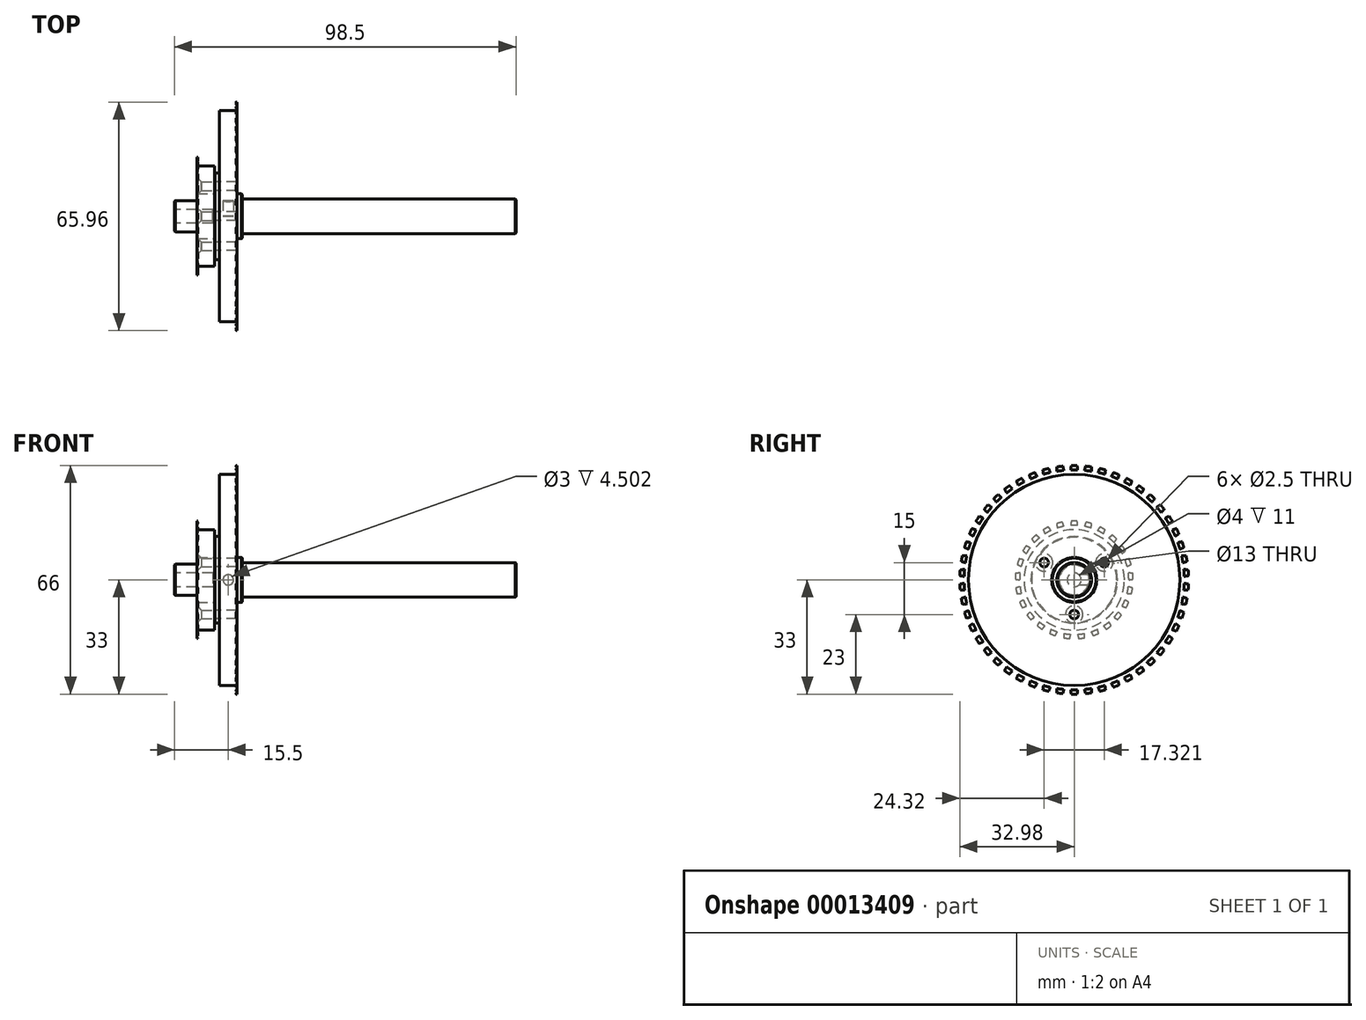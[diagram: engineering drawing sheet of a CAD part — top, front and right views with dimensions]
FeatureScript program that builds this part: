
annotation { "Feature Type Name" : "Feature", "Feature Type Description" : "" }
export const myFeature = defineFeature(function(context is Context, id is Id, definition is map)
    precondition{}
    {
        {
            var Q0;
            Q0=qCreatedBy(makeId("Right.planeOp"),FACE);
            var sketch = newSketch(context, id + "F0", { "sketchPlane" : qUnion([Q0])});
            skCircle(sketch, "E0", {"center": v(0, 0) * mm, "radius": 4.5 * mm});
            skCircle(sketch, "E1", {"center": v(0, 0) * mm, "radius": 5 * mm});
            skSolve(sketch);
        }
        {
            var Q0;
            Q0=makeQuery(id+"F0.imprint","IMPRINT",FACE,{"disambiguationData":[TD([[makeQuery(id+"F0.imprint","IMPRINT",EDGE,{"derivedFrom":sQuery(id+"F0.wireOp",EDGE,"E0")}),1.0]])]});
            extrude(context, id + "F1", {"entities" : qUnion([Q0]), "oppositeDirection" : true, "depth" : 13 * mm});
        }
        {
            var Q0;
            Q0=makeQuery(id+"F0.imprint","IMPRINT",FACE,{"disambiguationData":[TD([[makeQuery(id+"F0.imprint","IMPRINT",EDGE,{"derivedFrom":sQuery(id+"F0.wireOp",EDGE,"E0")}),1.0]])]});
            var Q1;
            Q1=makeQuery(id+"F0.imprint","IMPRINT",FACE,{"disambiguationData":[TD([[makeQuery(id+"F0.imprint","IMPRINT",EDGE,{"derivedFrom":sQuery(id+"F0.wireOp",EDGE,"E0")}),-1.0]])]});
            extrude(context, id + "F2", {"entities" : qUnion([Q0, Q1]), "operationType" : NewBodyOperationType.ADD, "depth" : 85.5 * mm});
        }
        {
            var Q0;
            Q0=makeQuery(id+"F1.opExtrude","CAP_FACE",FACE,{"disambiguationData":[OSD([sQuery(id+"F0.wireOp",EDGE,"E0")])],"isStart":false});
            var sketch = newSketch(context, id + "F3", { "sketchPlane" : qUnion([Q0])});
            skCircle(sketch, "E2", {"center": v(0, 0) * mm, "radius": 2 * mm});
            skSolve(sketch);
        }
        {
            var Q0;
            Q0=makeQuery(id+"F3.imprint","IMPRINT",FACE,{"disambiguationData":[TD([[makeQuery(id+"F3.imprint","IMPRINT",EDGE,{"derivedFrom":sQuery(id+"F3.wireOp",EDGE,"E2")}),1.0]])]});
            extrude(context, id + "F4", {"entities" : qUnion([Q0]), "operationType" : NewBodyOperationType.REMOVE, "oppositeDirection" : true, "depth" : 11 * mm});
        }
        {
            var Q0;
            Q0=makeQuery(id+"F2.opExtrude","CAP_FACE",FACE,{"disambiguationData":[OSD([sQuery(id+"F0.wireOp",EDGE,"E1")])],"isStart":true});
            var sketch = newSketch(context, id + "F5", { "sketchPlane" : qUnion([Q0])});
            skCircle(sketch, "E3", {"center": v(0, 0) * mm, "radius": 8 * mm});
            skSolve(sketch);
        }
        {
            var Q0;
            Q0=makeQuery(id+"F5.imprint","IMPRINT",FACE,{"disambiguationData":[TD([[makeQuery(id+"F5.imprint","IMPRINT",EDGE,{"derivedFrom":sQuery(id+"F5.wireOp",EDGE,"E3")}),1.0]])]});
            extrude(context, id + "F6", {"entities" : qUnion([Q0]), "oppositeDirection" : true, "depth" : 5 * mm});
        }
        {
            var Q0;
            Q0=qCreatedBy(makeId("Front.planeOp"),FACE);
            var sketch = newSketch(context, id + "F7", { "sketchPlane" : qUnion([Q0])});
            skLineSegment(sketch, "E4.0", {"start": v(0, -8) * mm, "end": v(0, 8) * mm});
            skLineSegment(sketch, "E4.1", {"start": v(5, -8) * mm, "end": v(5, 8) * mm});
            skLineSegment(sketch, "E5", {"start": v(5, 0) * mm, "end": v(0, 0) * mm, "construction": true});
            skCircle(sketch, "E6", {"center": v(2.5, 0) * mm, "radius": 1.5 * mm});
            skSolve(sketch);
        }
        {
            var Q0;
            Q0=makeQuery(id+"F7.imprint","IMPRINT",FACE,{"disambiguationData":[TD([[makeQuery(id+"F7.imprint","IMPRINT",EDGE,{"derivedFrom":sQuery(id+"F7.wireOp",EDGE,"E6")}),1.0]])]});
            extrude(context, id + "F8", {"entities" : qUnion([Q0]), "operationType" : NewBodyOperationType.REMOVE, "oppositeDirection" : true, "depth" : 8 * mm});
        }
        {
            var Q0;
            Q0=makeQuery(id+"F6.opExtrude","CAP_FACE",FACE,{"disambiguationData":[OSD([sQuery(id+"F0.wireOp",EDGE,"E1"),sQuery(id+"F5.wireOp",EDGE,"E3")])],"isStart":true});
            var sketch = newSketch(context, id + "F9", { "sketchPlane" : qUnion([Q0])});
            skCircle(sketch, "E7", {"center": v(0, 0) * mm, "radius": 30.5 * mm});
            skCircle(sketch, "E8", {"center": v(0, 0) * mm, "radius": 33 * mm});
            skCircle(sketch, "E9", {"center": v(0, 0) * mm, "radius": 31.75 * mm, "construction": true});
            skLineSegment(sketch, "E10", {"start": v(0, 0) * mm, "end": v(0, 33) * mm, "construction": true});
            skLineSegment(sketch, "E11", {"start": v(0, 0) * mm, "end": v(-1, 31.73) * mm, "construction": true});
            skLineSegment(sketch, "E12", {"start": v(0, 0) * mm, "end": v(0, -10) * mm, "construction": true});
            skCircle(sketch, "E13", {"center": v(0, -10) * mm, "radius": 1.25 * mm});
            skCircle(sketch, "E14.1.0", {"center": v(8.66, 5) * mm, "radius": 1.25 * mm});
            skCircle(sketch, "E14.2.0", {"center": v(-8.66, 5) * mm, "radius": 1.25 * mm});
            skLineSegment(sketch, "E15", {"start": v(0, 30.5) * mm, "end": v(15, 30.5) * mm, "construction": true});
            skArc(sketch, "E16", {"start": v(-0.85, 32.99) * mm, "mid": v(-1, 31.74) * mm, "end": v(-1.04, 30.48) * mm});
            skArc(sketch, "E17.0.MirrorCS", {"start": v(0.85, 32.99) * mm, "mid": v(1, 31.74) * mm, "end": v(1.04, 30.48) * mm});
            skArc(sketch, "E18.1.0", {"start": v(-4.98, 32.62) * mm, "mid": v(-4.97, 31.36) * mm, "end": v(-4.86, 30.11) * mm});
            skArc(sketch, "E18.1.1", {"start": v(-3.3, 32.84) * mm, "mid": v(-2.99, 31.61) * mm, "end": v(-2.78, 30.37) * mm});
            skArc(sketch, "E18.2.0", {"start": v(-9.03, 31.74) * mm, "mid": v(-8.86, 30.5) * mm, "end": v(-8.6, 29.26) * mm});
            skArc(sketch, "E18.2.1", {"start": v(-7.38, 32.16) * mm, "mid": v(-6.93, 31) * mm, "end": v(-6.57, 29.78) * mm});
            skArc(sketch, "E18.3.0", {"start": v(-12.93, 30.36) * mm, "mid": v(-12.61, 29.14) * mm, "end": v(-12.2, 27.96) * mm});
            skArc(sketch, "E18.3.1", {"start": v(-11.35, 30.99) * mm, "mid": v(-10.76, 29.88) * mm, "end": v(-10.25, 28.73) * mm});
            skArc(sketch, "E18.4.0", {"start": v(-16.64, 28.5) * mm, "mid": v(-16.16, 27.33) * mm, "end": v(-15.6, 26.2) * mm});
            skArc(sketch, "E18.4.1", {"start": v(-15.15, 29.32) * mm, "mid": v(-14.42, 28.3) * mm, "end": v(-13.77, 27.22) * mm});
            skArc(sketch, "E18.5.0", {"start": v(-20.08, 26.19) * mm, "mid": v(-19.46, 25.1) * mm, "end": v(-18.76, 24.05) * mm});
            skArc(sketch, "E18.5.1", {"start": v(-18.7, 27.19) * mm, "mid": v(-17.85, 26.26) * mm, "end": v(-17.07, 25.27) * mm});
            skArc(sketch, "E18.6.0", {"start": v(-23.2, 23.47) * mm, "mid": v(-22.45, 22.45) * mm, "end": v(-21.63, 21.5) * mm});
            skArc(sketch, "E18.6.1", {"start": v(-21.96, 24.63) * mm, "mid": v(-21, 23.82) * mm, "end": v(-20.1, 22.94) * mm});
            skArc(sketch, "E18.7.0", {"start": v(-25.96, 20.37) * mm, "mid": v(-25.1, 19.46) * mm, "end": v(-24.15, 18.62) * mm});
            skArc(sketch, "E18.7.1", {"start": v(-24.88, 21.68) * mm, "mid": v(-23.82, 21) * mm, "end": v(-22.82, 20.24) * mm});
            skArc(sketch, "E18.8.0", {"start": v(-28.3, 16.96) * mm, "mid": v(-27.33, 16.17) * mm, "end": v(-26.3, 15.45) * mm});
            skArc(sketch, "E18.8.1", {"start": v(-27.4, 18.4) * mm, "mid": v(-26.26, 17.85) * mm, "end": v(-25.18, 17.22) * mm});
            skArc(sketch, "E18.9.0", {"start": v(-30.21, 13.28) * mm, "mid": v(-29.14, 12.61) * mm, "end": v(-28.03, 12.03) * mm});
            skArc(sketch, "E18.9.1", {"start": v(-29.49, 14.82) * mm, "mid": v(-28.3, 14.42) * mm, "end": v(-27.14, 13.92) * mm});
            skArc(sketch, "E18.10.0", {"start": v(-31.64, 9.39) * mm, "mid": v(-30.5, 8.86) * mm, "end": v(-29.31, 8.43) * mm});
            skArc(sketch, "E18.10.1", {"start": v(-31.11, 11) * mm, "mid": v(-29.88, 10.76) * mm, "end": v(-28.67, 10.41) * mm});
            skArc(sketch, "E18.11.0", {"start": v(-32.56, 5.35) * mm, "mid": v(-31.36, 4.97) * mm, "end": v(-30.14, 4.69) * mm});
            skArc(sketch, "E18.11.1", {"start": v(-32.25, 7.02) * mm, "mid": v(-31, 6.93) * mm, "end": v(-29.75, 6.74) * mm});
            skArc(sketch, "E18.12.0", {"start": v(-32.98, 1.22) * mm, "mid": v(-31.74, 1) * mm, "end": v(-30.49, 0.87) * mm});
            skArc(sketch, "E18.12.1", {"start": v(-32.87, 2.92) * mm, "mid": v(-31.61, 2.99) * mm, "end": v(-30.36, 2.96) * mm});
            skArc(sketch, "E18.13.0", {"start": v(-32.87, -2.92) * mm, "mid": v(-31.61, -2.99) * mm, "end": v(-30.36, -2.96) * mm});
            skArc(sketch, "E18.13.1", {"start": v(-32.98, -1.22) * mm, "mid": v(-31.74, -1) * mm, "end": v(-30.49, -0.87) * mm});
            skArc(sketch, "E18.14.0", {"start": v(-32.25, -7.02) * mm, "mid": v(-31, -6.93) * mm, "end": v(-29.75, -6.74) * mm});
            skArc(sketch, "E18.14.1", {"start": v(-32.56, -5.35) * mm, "mid": v(-31.36, -4.97) * mm, "end": v(-30.14, -4.69) * mm});
            skArc(sketch, "E18.15.0", {"start": v(-31.11, -11) * mm, "mid": v(-29.88, -10.76) * mm, "end": v(-28.67, -10.41) * mm});
            skArc(sketch, "E18.15.1", {"start": v(-31.64, -9.39) * mm, "mid": v(-30.5, -8.86) * mm, "end": v(-29.31, -8.43) * mm});
            skArc(sketch, "E18.16.0", {"start": v(-29.49, -14.82) * mm, "mid": v(-28.3, -14.42) * mm, "end": v(-27.14, -13.92) * mm});
            skArc(sketch, "E18.16.1", {"start": v(-30.21, -13.28) * mm, "mid": v(-29.14, -12.61) * mm, "end": v(-28.03, -12.03) * mm});
            skArc(sketch, "E18.17.0", {"start": v(-27.4, -18.4) * mm, "mid": v(-26.26, -17.85) * mm, "end": v(-25.18, -17.22) * mm});
            skArc(sketch, "E18.17.1", {"start": v(-28.3, -16.96) * mm, "mid": v(-27.33, -16.17) * mm, "end": v(-26.3, -15.45) * mm});
            skArc(sketch, "E18.18.0", {"start": v(-24.88, -21.68) * mm, "mid": v(-23.82, -21) * mm, "end": v(-22.82, -20.24) * mm});
            skArc(sketch, "E18.18.1", {"start": v(-25.96, -20.37) * mm, "mid": v(-25.1, -19.46) * mm, "end": v(-24.15, -18.62) * mm});
            skArc(sketch, "E18.19.0", {"start": v(-21.96, -24.63) * mm, "mid": v(-21, -23.82) * mm, "end": v(-20.1, -22.94) * mm});
            skArc(sketch, "E18.19.1", {"start": v(-23.2, -23.47) * mm, "mid": v(-22.45, -22.45) * mm, "end": v(-21.63, -21.5) * mm});
            skArc(sketch, "E18.20.0", {"start": v(-18.7, -27.19) * mm, "mid": v(-17.85, -26.26) * mm, "end": v(-17.07, -25.27) * mm});
            skArc(sketch, "E18.20.1", {"start": v(-20.08, -26.19) * mm, "mid": v(-19.46, -25.1) * mm, "end": v(-18.76, -24.05) * mm});
            skArc(sketch, "E18.21.0", {"start": v(-15.15, -29.32) * mm, "mid": v(-14.42, -28.3) * mm, "end": v(-13.77, -27.22) * mm});
            skArc(sketch, "E18.21.1", {"start": v(-16.64, -28.5) * mm, "mid": v(-16.16, -27.33) * mm, "end": v(-15.6, -26.2) * mm});
            skArc(sketch, "E18.22.0", {"start": v(-11.35, -30.99) * mm, "mid": v(-10.76, -29.88) * mm, "end": v(-10.25, -28.73) * mm});
            skArc(sketch, "E18.22.1", {"start": v(-12.93, -30.36) * mm, "mid": v(-12.61, -29.14) * mm, "end": v(-12.2, -27.96) * mm});
            skArc(sketch, "E18.23.0", {"start": v(-7.38, -32.16) * mm, "mid": v(-6.93, -31) * mm, "end": v(-6.57, -29.78) * mm});
            skArc(sketch, "E18.23.1", {"start": v(-9.03, -31.74) * mm, "mid": v(-8.86, -30.5) * mm, "end": v(-8.6, -29.26) * mm});
            skArc(sketch, "E18.24.0", {"start": v(-3.3, -32.84) * mm, "mid": v(-2.99, -31.61) * mm, "end": v(-2.78, -30.37) * mm});
            skArc(sketch, "E18.24.1", {"start": v(-4.98, -32.62) * mm, "mid": v(-4.97, -31.36) * mm, "end": v(-4.86, -30.11) * mm});
            skArc(sketch, "E18.25.0", {"start": v(0.85, -32.99) * mm, "mid": v(1, -31.74) * mm, "end": v(1.04, -30.48) * mm});
            skArc(sketch, "E18.25.1", {"start": v(-0.85, -32.99) * mm, "mid": v(-1, -31.74) * mm, "end": v(-1.04, -30.48) * mm});
            skArc(sketch, "E18.26.0", {"start": v(4.98, -32.62) * mm, "mid": v(4.97, -31.36) * mm, "end": v(4.86, -30.11) * mm});
            skArc(sketch, "E18.26.1", {"start": v(3.3, -32.84) * mm, "mid": v(2.99, -31.61) * mm, "end": v(2.78, -30.37) * mm});
            skArc(sketch, "E18.27.0", {"start": v(9.03, -31.74) * mm, "mid": v(8.86, -30.5) * mm, "end": v(8.6, -29.26) * mm});
            skArc(sketch, "E18.27.1", {"start": v(7.38, -32.16) * mm, "mid": v(6.93, -31) * mm, "end": v(6.57, -29.78) * mm});
            skArc(sketch, "E18.28.0", {"start": v(12.93, -30.36) * mm, "mid": v(12.61, -29.14) * mm, "end": v(12.2, -27.96) * mm});
            skArc(sketch, "E18.28.1", {"start": v(11.35, -30.99) * mm, "mid": v(10.76, -29.88) * mm, "end": v(10.25, -28.73) * mm});
            skArc(sketch, "E18.29.0", {"start": v(16.64, -28.5) * mm, "mid": v(16.16, -27.33) * mm, "end": v(15.6, -26.2) * mm});
            skArc(sketch, "E18.29.1", {"start": v(15.15, -29.32) * mm, "mid": v(14.42, -28.3) * mm, "end": v(13.77, -27.22) * mm});
            skArc(sketch, "E18.30.0", {"start": v(20.08, -26.19) * mm, "mid": v(19.46, -25.1) * mm, "end": v(18.76, -24.05) * mm});
            skArc(sketch, "E18.30.1", {"start": v(18.7, -27.19) * mm, "mid": v(17.85, -26.26) * mm, "end": v(17.07, -25.27) * mm});
            skArc(sketch, "E18.31.0", {"start": v(23.2, -23.47) * mm, "mid": v(22.45, -22.45) * mm, "end": v(21.63, -21.5) * mm});
            skArc(sketch, "E18.31.1", {"start": v(21.96, -24.63) * mm, "mid": v(21, -23.82) * mm, "end": v(20.1, -22.94) * mm});
            skArc(sketch, "E18.32.0", {"start": v(25.96, -20.37) * mm, "mid": v(25.1, -19.46) * mm, "end": v(24.15, -18.62) * mm});
            skArc(sketch, "E18.32.1", {"start": v(24.88, -21.68) * mm, "mid": v(23.82, -21) * mm, "end": v(22.82, -20.24) * mm});
            skArc(sketch, "E18.33.0", {"start": v(28.3, -16.96) * mm, "mid": v(27.33, -16.17) * mm, "end": v(26.3, -15.45) * mm});
            skArc(sketch, "E18.33.1", {"start": v(27.4, -18.4) * mm, "mid": v(26.26, -17.85) * mm, "end": v(25.18, -17.22) * mm});
            skArc(sketch, "E18.34.0", {"start": v(30.21, -13.28) * mm, "mid": v(29.14, -12.61) * mm, "end": v(28.03, -12.03) * mm});
            skArc(sketch, "E18.34.1", {"start": v(29.49, -14.82) * mm, "mid": v(28.3, -14.42) * mm, "end": v(27.14, -13.92) * mm});
            skArc(sketch, "E18.35.0", {"start": v(31.64, -9.39) * mm, "mid": v(30.5, -8.86) * mm, "end": v(29.31, -8.43) * mm});
            skArc(sketch, "E18.35.1", {"start": v(31.11, -11) * mm, "mid": v(29.88, -10.76) * mm, "end": v(28.67, -10.41) * mm});
            skArc(sketch, "E18.36.0", {"start": v(32.56, -5.35) * mm, "mid": v(31.36, -4.97) * mm, "end": v(30.14, -4.69) * mm});
            skArc(sketch, "E18.36.1", {"start": v(32.25, -7.02) * mm, "mid": v(31, -6.93) * mm, "end": v(29.75, -6.74) * mm});
            skArc(sketch, "E18.37.0", {"start": v(32.98, -1.22) * mm, "mid": v(31.74, -1) * mm, "end": v(30.49, -0.87) * mm});
            skArc(sketch, "E18.37.1", {"start": v(32.87, -2.92) * mm, "mid": v(31.61, -2.99) * mm, "end": v(30.36, -2.96) * mm});
            skArc(sketch, "E18.38.0", {"start": v(32.87, 2.92) * mm, "mid": v(31.61, 2.99) * mm, "end": v(30.36, 2.96) * mm});
            skArc(sketch, "E18.38.1", {"start": v(32.98, 1.22) * mm, "mid": v(31.74, 1) * mm, "end": v(30.49, 0.87) * mm});
            skArc(sketch, "E18.39.0", {"start": v(32.25, 7.02) * mm, "mid": v(31, 6.93) * mm, "end": v(29.75, 6.74) * mm});
            skArc(sketch, "E18.39.1", {"start": v(32.56, 5.35) * mm, "mid": v(31.36, 4.97) * mm, "end": v(30.14, 4.69) * mm});
            skArc(sketch, "E18.40.0", {"start": v(31.11, 11) * mm, "mid": v(29.88, 10.76) * mm, "end": v(28.67, 10.41) * mm});
            skArc(sketch, "E18.40.1", {"start": v(31.64, 9.39) * mm, "mid": v(30.5, 8.86) * mm, "end": v(29.31, 8.43) * mm});
            skArc(sketch, "E18.41.0", {"start": v(29.49, 14.82) * mm, "mid": v(28.3, 14.42) * mm, "end": v(27.14, 13.92) * mm});
            skArc(sketch, "E18.41.1", {"start": v(30.21, 13.28) * mm, "mid": v(29.14, 12.61) * mm, "end": v(28.03, 12.03) * mm});
            skArc(sketch, "E18.42.0", {"start": v(27.4, 18.4) * mm, "mid": v(26.26, 17.85) * mm, "end": v(25.18, 17.22) * mm});
            skArc(sketch, "E18.42.1", {"start": v(28.3, 16.96) * mm, "mid": v(27.33, 16.17) * mm, "end": v(26.3, 15.45) * mm});
            skArc(sketch, "E18.43.0", {"start": v(24.88, 21.68) * mm, "mid": v(23.82, 21) * mm, "end": v(22.82, 20.24) * mm});
            skArc(sketch, "E18.43.1", {"start": v(25.96, 20.37) * mm, "mid": v(25.1, 19.46) * mm, "end": v(24.15, 18.62) * mm});
            skArc(sketch, "E18.44.0", {"start": v(21.96, 24.63) * mm, "mid": v(21, 23.82) * mm, "end": v(20.1, 22.94) * mm});
            skArc(sketch, "E18.44.1", {"start": v(23.2, 23.47) * mm, "mid": v(22.45, 22.45) * mm, "end": v(21.63, 21.5) * mm});
            skArc(sketch, "E18.45.0", {"start": v(18.7, 27.19) * mm, "mid": v(17.85, 26.26) * mm, "end": v(17.07, 25.27) * mm});
            skArc(sketch, "E18.45.1", {"start": v(20.08, 26.19) * mm, "mid": v(19.46, 25.1) * mm, "end": v(18.76, 24.05) * mm});
            skArc(sketch, "E18.46.0", {"start": v(15.15, 29.32) * mm, "mid": v(14.42, 28.3) * mm, "end": v(13.77, 27.22) * mm});
            skArc(sketch, "E18.46.1", {"start": v(16.64, 28.5) * mm, "mid": v(16.16, 27.33) * mm, "end": v(15.6, 26.2) * mm});
            skArc(sketch, "E18.47.0", {"start": v(11.35, 30.99) * mm, "mid": v(10.76, 29.88) * mm, "end": v(10.25, 28.73) * mm});
            skArc(sketch, "E18.47.1", {"start": v(12.93, 30.36) * mm, "mid": v(12.61, 29.14) * mm, "end": v(12.2, 27.96) * mm});
            skArc(sketch, "E18.48.0", {"start": v(7.38, 32.16) * mm, "mid": v(6.93, 31) * mm, "end": v(6.57, 29.78) * mm});
            skArc(sketch, "E18.48.1", {"start": v(9.03, 31.74) * mm, "mid": v(8.86, 30.5) * mm, "end": v(8.6, 29.26) * mm});
            skArc(sketch, "E18.49.0", {"start": v(3.3, 32.84) * mm, "mid": v(2.99, 31.61) * mm, "end": v(2.78, 30.37) * mm});
            skArc(sketch, "E18.49.1", {"start": v(4.98, 32.62) * mm, "mid": v(4.97, 31.36) * mm, "end": v(4.86, 30.11) * mm});
            skSolve(sketch);
        }
        {
            var Q0;
            Q0=makeQuery(id+"F9.imprint","IMPRINT",FACE,{"disambiguationData":[TD([[makeQuery(id+"F9.imprint","IMPRINT",EDGE,{"derivedFrom":sQuery(id+"F9.wireOp",EDGE,"E13")}),-1.0]])]});
            var Q1;
            {var subQ1=sQuery(id+"F9.wireOp",EDGE,"E16");Q1=makeQuery(id+"F9.imprint","IMPRINT",FACE,{"disambiguationData":[TD([[makeQuery(id+"F9.imprint","IMPRINT",EDGE,{"derivedFrom":subQ1}),1.0]])]});}
            var Q2;
            {var subQ1=sQuery(id+"F9.wireOp",EDGE,"E18.1.0");Q2=makeQuery(id+"F9.imprint","IMPRINT",FACE,{"disambiguationData":[TD([[makeQuery(id+"F9.imprint","IMPRINT",EDGE,{"derivedFrom":subQ1}),1.0]])]});}
            var Q3;
            {var subQ1=sQuery(id+"F9.wireOp",EDGE,"E18.2.0");Q3=makeQuery(id+"F9.imprint","IMPRINT",FACE,{"disambiguationData":[TD([[makeQuery(id+"F9.imprint","IMPRINT",EDGE,{"derivedFrom":subQ1}),1.0]])]});}
            var Q4;
            {var subQ2=sQuery(id+"F9.wireOp",EDGE,"E18.3.0");Q4=makeQuery(id+"F9.imprint","IMPRINT",FACE,{"disambiguationData":[TD([[makeQuery(id+"F9.imprint","IMPRINT",EDGE,{"derivedFrom":subQ2}),1.0]])]});}
            var Q5;
            {var subQ1=sQuery(id+"F9.wireOp",EDGE,"E18.4.0");Q5=makeQuery(id+"F9.imprint","IMPRINT",FACE,{"disambiguationData":[TD([[makeQuery(id+"F9.imprint","IMPRINT",EDGE,{"derivedFrom":subQ1}),1.0]])]});}
            var Q6;
            {var subQ1=sQuery(id+"F9.wireOp",EDGE,"E18.5.0");Q6=makeQuery(id+"F9.imprint","IMPRINT",FACE,{"disambiguationData":[TD([[makeQuery(id+"F9.imprint","IMPRINT",EDGE,{"derivedFrom":subQ1}),1.0]])]});}
            var Q7;
            {var subQ1=sQuery(id+"F9.wireOp",EDGE,"E18.6.0");Q7=makeQuery(id+"F9.imprint","IMPRINT",FACE,{"disambiguationData":[TD([[makeQuery(id+"F9.imprint","IMPRINT",EDGE,{"derivedFrom":subQ1}),1.0]])]});}
            var Q8;
            {var subQ1=sQuery(id+"F9.wireOp",EDGE,"E18.7.0");Q8=makeQuery(id+"F9.imprint","IMPRINT",FACE,{"disambiguationData":[TD([[makeQuery(id+"F9.imprint","IMPRINT",EDGE,{"derivedFrom":subQ1}),1.0]])]});}
            var Q9;
            {var subQ1=sQuery(id+"F9.wireOp",EDGE,"E18.8.0");Q9=makeQuery(id+"F9.imprint","IMPRINT",FACE,{"disambiguationData":[TD([[makeQuery(id+"F9.imprint","IMPRINT",EDGE,{"derivedFrom":subQ1}),1.0]])]});}
            var Q10;
            {var subQ1=sQuery(id+"F9.wireOp",EDGE,"E18.9.0");Q10=makeQuery(id+"F9.imprint","IMPRINT",FACE,{"disambiguationData":[TD([[makeQuery(id+"F9.imprint","IMPRINT",EDGE,{"derivedFrom":subQ1}),1.0]])]});}
            var Q11;
            {var subQ1=sQuery(id+"F9.wireOp",EDGE,"E18.10.0");Q11=makeQuery(id+"F9.imprint","IMPRINT",FACE,{"disambiguationData":[TD([[makeQuery(id+"F9.imprint","IMPRINT",EDGE,{"derivedFrom":subQ1}),1.0]])]});}
            var Q12;
            {var subQ1=sQuery(id+"F9.wireOp",EDGE,"E18.11.0");Q12=makeQuery(id+"F9.imprint","IMPRINT",FACE,{"disambiguationData":[TD([[makeQuery(id+"F9.imprint","IMPRINT",EDGE,{"derivedFrom":subQ1}),1.0]])]});}
            var Q13;
            {var subQ1=sQuery(id+"F9.wireOp",EDGE,"E18.12.0");Q13=makeQuery(id+"F9.imprint","IMPRINT",FACE,{"disambiguationData":[TD([[makeQuery(id+"F9.imprint","IMPRINT",EDGE,{"derivedFrom":subQ1}),1.0]])]});}
            var Q14;
            {var subQ1=sQuery(id+"F9.wireOp",EDGE,"E18.13.0");Q14=makeQuery(id+"F9.imprint","IMPRINT",FACE,{"disambiguationData":[TD([[makeQuery(id+"F9.imprint","IMPRINT",EDGE,{"derivedFrom":subQ1}),1.0]])]});}
            var Q15;
            {var subQ1=sQuery(id+"F9.wireOp",EDGE,"E18.14.0");Q15=makeQuery(id+"F9.imprint","IMPRINT",FACE,{"disambiguationData":[TD([[makeQuery(id+"F9.imprint","IMPRINT",EDGE,{"derivedFrom":subQ1}),1.0]])]});}
            var Q16;
            {var subQ1=sQuery(id+"F9.wireOp",EDGE,"E18.15.0");Q16=makeQuery(id+"F9.imprint","IMPRINT",FACE,{"disambiguationData":[TD([[makeQuery(id+"F9.imprint","IMPRINT",EDGE,{"derivedFrom":subQ1}),1.0]])]});}
            var Q17;
            {var subQ1=sQuery(id+"F9.wireOp",EDGE,"E18.16.0");Q17=makeQuery(id+"F9.imprint","IMPRINT",FACE,{"disambiguationData":[TD([[makeQuery(id+"F9.imprint","IMPRINT",EDGE,{"derivedFrom":subQ1}),1.0]])]});}
            var Q18;
            {var subQ1=sQuery(id+"F9.wireOp",EDGE,"E18.17.0");Q18=makeQuery(id+"F9.imprint","IMPRINT",FACE,{"disambiguationData":[TD([[makeQuery(id+"F9.imprint","IMPRINT",EDGE,{"derivedFrom":subQ1}),1.0]])]});}
            var Q19;
            {var subQ1=sQuery(id+"F9.wireOp",EDGE,"E18.18.0");Q19=makeQuery(id+"F9.imprint","IMPRINT",FACE,{"disambiguationData":[TD([[makeQuery(id+"F9.imprint","IMPRINT",EDGE,{"derivedFrom":subQ1}),1.0]])]});}
            var Q20;
            {var subQ2=sQuery(id+"F9.wireOp",EDGE,"E18.19.0");Q20=makeQuery(id+"F9.imprint","IMPRINT",FACE,{"disambiguationData":[TD([[makeQuery(id+"F9.imprint","IMPRINT",EDGE,{"derivedFrom":subQ2}),1.0]])]});}
            var Q21;
            {var subQ1=sQuery(id+"F9.wireOp",EDGE,"E18.20.0");Q21=makeQuery(id+"F9.imprint","IMPRINT",FACE,{"disambiguationData":[TD([[makeQuery(id+"F9.imprint","IMPRINT",EDGE,{"derivedFrom":subQ1}),1.0]])]});}
            var Q22;
            {var subQ1=sQuery(id+"F9.wireOp",EDGE,"E18.21.0");Q22=makeQuery(id+"F9.imprint","IMPRINT",FACE,{"disambiguationData":[TD([[makeQuery(id+"F9.imprint","IMPRINT",EDGE,{"derivedFrom":subQ1}),1.0]])]});}
            var Q23;
            {var subQ1=sQuery(id+"F9.wireOp",EDGE,"E18.22.0");Q23=makeQuery(id+"F9.imprint","IMPRINT",FACE,{"disambiguationData":[TD([[makeQuery(id+"F9.imprint","IMPRINT",EDGE,{"derivedFrom":subQ1}),1.0]])]});}
            var Q24;
            {var subQ1=sQuery(id+"F9.wireOp",EDGE,"E18.23.0");Q24=makeQuery(id+"F9.imprint","IMPRINT",FACE,{"disambiguationData":[TD([[makeQuery(id+"F9.imprint","IMPRINT",EDGE,{"derivedFrom":subQ1}),1.0]])]});}
            var Q25;
            {var subQ1=sQuery(id+"F9.wireOp",EDGE,"E18.24.0");Q25=makeQuery(id+"F9.imprint","IMPRINT",FACE,{"disambiguationData":[TD([[makeQuery(id+"F9.imprint","IMPRINT",EDGE,{"derivedFrom":subQ1}),1.0]])]});}
            var Q26;
            {var subQ1=sQuery(id+"F9.wireOp",EDGE,"E18.25.0");Q26=makeQuery(id+"F9.imprint","IMPRINT",FACE,{"disambiguationData":[TD([[makeQuery(id+"F9.imprint","IMPRINT",EDGE,{"derivedFrom":subQ1}),1.0]])]});}
            var Q27;
            {var subQ1=sQuery(id+"F9.wireOp",EDGE,"E18.26.0");Q27=makeQuery(id+"F9.imprint","IMPRINT",FACE,{"disambiguationData":[TD([[makeQuery(id+"F9.imprint","IMPRINT",EDGE,{"derivedFrom":subQ1}),1.0]])]});}
            var Q28;
            {var subQ2=sQuery(id+"F9.wireOp",EDGE,"E18.27.0");Q28=makeQuery(id+"F9.imprint","IMPRINT",FACE,{"disambiguationData":[TD([[makeQuery(id+"F9.imprint","IMPRINT",EDGE,{"derivedFrom":subQ2}),1.0]])]});}
            var Q29;
            {var subQ1=sQuery(id+"F9.wireOp",EDGE,"E18.28.0");Q29=makeQuery(id+"F9.imprint","IMPRINT",FACE,{"disambiguationData":[TD([[makeQuery(id+"F9.imprint","IMPRINT",EDGE,{"derivedFrom":subQ1}),1.0]])]});}
            var Q30;
            {var subQ1=sQuery(id+"F9.wireOp",EDGE,"E18.29.0");Q30=makeQuery(id+"F9.imprint","IMPRINT",FACE,{"disambiguationData":[TD([[makeQuery(id+"F9.imprint","IMPRINT",EDGE,{"derivedFrom":subQ1}),1.0]])]});}
            var Q31;
            {var subQ1=sQuery(id+"F9.wireOp",EDGE,"E18.30.0");Q31=makeQuery(id+"F9.imprint","IMPRINT",FACE,{"disambiguationData":[TD([[makeQuery(id+"F9.imprint","IMPRINT",EDGE,{"derivedFrom":subQ1}),1.0]])]});}
            var Q32;
            {var subQ1=sQuery(id+"F9.wireOp",EDGE,"E18.31.0");Q32=makeQuery(id+"F9.imprint","IMPRINT",FACE,{"disambiguationData":[TD([[makeQuery(id+"F9.imprint","IMPRINT",EDGE,{"derivedFrom":subQ1}),1.0]])]});}
            var Q33;
            {var subQ1=sQuery(id+"F9.wireOp",EDGE,"E18.32.0");Q33=makeQuery(id+"F9.imprint","IMPRINT",FACE,{"disambiguationData":[TD([[makeQuery(id+"F9.imprint","IMPRINT",EDGE,{"derivedFrom":subQ1}),1.0]])]});}
            var Q34;
            {var subQ1=sQuery(id+"F9.wireOp",EDGE,"E18.33.0");Q34=makeQuery(id+"F9.imprint","IMPRINT",FACE,{"disambiguationData":[TD([[makeQuery(id+"F9.imprint","IMPRINT",EDGE,{"derivedFrom":subQ1}),1.0]])]});}
            var Q35;
            {var subQ1=sQuery(id+"F9.wireOp",EDGE,"E18.34.0");Q35=makeQuery(id+"F9.imprint","IMPRINT",FACE,{"disambiguationData":[TD([[makeQuery(id+"F9.imprint","IMPRINT",EDGE,{"derivedFrom":subQ1}),1.0]])]});}
            var Q36;
            {var subQ2=sQuery(id+"F9.wireOp",EDGE,"E18.35.0");Q36=makeQuery(id+"F9.imprint","IMPRINT",FACE,{"disambiguationData":[TD([[makeQuery(id+"F9.imprint","IMPRINT",EDGE,{"derivedFrom":subQ2}),1.0]])]});}
            var Q37;
            {var subQ1=sQuery(id+"F9.wireOp",EDGE,"E18.36.0");Q37=makeQuery(id+"F9.imprint","IMPRINT",FACE,{"disambiguationData":[TD([[makeQuery(id+"F9.imprint","IMPRINT",EDGE,{"derivedFrom":subQ1}),1.0]])]});}
            var Q38;
            {var subQ1=sQuery(id+"F9.wireOp",EDGE,"E18.37.0");Q38=makeQuery(id+"F9.imprint","IMPRINT",FACE,{"disambiguationData":[TD([[makeQuery(id+"F9.imprint","IMPRINT",EDGE,{"derivedFrom":subQ1}),1.0]])]});}
            var Q39;
            {var subQ1=sQuery(id+"F9.wireOp",EDGE,"E18.38.0");Q39=makeQuery(id+"F9.imprint","IMPRINT",FACE,{"disambiguationData":[TD([[makeQuery(id+"F9.imprint","IMPRINT",EDGE,{"derivedFrom":subQ1}),1.0]])]});}
            var Q40;
            {var subQ2=sQuery(id+"F9.wireOp",EDGE,"E18.39.0");Q40=makeQuery(id+"F9.imprint","IMPRINT",FACE,{"disambiguationData":[TD([[makeQuery(id+"F9.imprint","IMPRINT",EDGE,{"derivedFrom":subQ2}),1.0]])]});}
            var Q41;
            {var subQ2=sQuery(id+"F9.wireOp",EDGE,"E18.40.0");Q41=makeQuery(id+"F9.imprint","IMPRINT",FACE,{"disambiguationData":[TD([[makeQuery(id+"F9.imprint","IMPRINT",EDGE,{"derivedFrom":subQ2}),1.0]])]});}
            var Q42;
            {var subQ2=sQuery(id+"F9.wireOp",EDGE,"E18.41.0");Q42=makeQuery(id+"F9.imprint","IMPRINT",FACE,{"disambiguationData":[TD([[makeQuery(id+"F9.imprint","IMPRINT",EDGE,{"derivedFrom":subQ2}),1.0]])]});}
            var Q43;
            {var subQ1=sQuery(id+"F9.wireOp",EDGE,"E18.42.0");Q43=makeQuery(id+"F9.imprint","IMPRINT",FACE,{"disambiguationData":[TD([[makeQuery(id+"F9.imprint","IMPRINT",EDGE,{"derivedFrom":subQ1}),1.0]])]});}
            var Q44;
            {var subQ1=sQuery(id+"F9.wireOp",EDGE,"E18.43.0");Q44=makeQuery(id+"F9.imprint","IMPRINT",FACE,{"disambiguationData":[TD([[makeQuery(id+"F9.imprint","IMPRINT",EDGE,{"derivedFrom":subQ1}),1.0]])]});}
            var Q45;
            {var subQ1=sQuery(id+"F9.wireOp",EDGE,"E18.44.0");Q45=makeQuery(id+"F9.imprint","IMPRINT",FACE,{"disambiguationData":[TD([[makeQuery(id+"F9.imprint","IMPRINT",EDGE,{"derivedFrom":subQ1}),1.0]])]});}
            var Q46;
            {var subQ1=sQuery(id+"F9.wireOp",EDGE,"E18.45.0");Q46=makeQuery(id+"F9.imprint","IMPRINT",FACE,{"disambiguationData":[TD([[makeQuery(id+"F9.imprint","IMPRINT",EDGE,{"derivedFrom":subQ1}),1.0]])]});}
            var Q47;
            {var subQ1=sQuery(id+"F9.wireOp",EDGE,"E18.46.0");Q47=makeQuery(id+"F9.imprint","IMPRINT",FACE,{"disambiguationData":[TD([[makeQuery(id+"F9.imprint","IMPRINT",EDGE,{"derivedFrom":subQ1}),1.0]])]});}
            var Q48;
            {var subQ2=sQuery(id+"F9.wireOp",EDGE,"E18.47.0");Q48=makeQuery(id+"F9.imprint","IMPRINT",FACE,{"disambiguationData":[TD([[makeQuery(id+"F9.imprint","IMPRINT",EDGE,{"derivedFrom":subQ2}),1.0]])]});}
            var Q49;
            {var subQ2=sQuery(id+"F9.wireOp",EDGE,"E18.48.0");Q49=makeQuery(id+"F9.imprint","IMPRINT",FACE,{"disambiguationData":[TD([[makeQuery(id+"F9.imprint","IMPRINT",EDGE,{"derivedFrom":subQ2}),1.0]])]});}
            var Q50;
            {var subQ2=sQuery(id+"F9.wireOp",EDGE,"E18.49.0");Q50=makeQuery(id+"F9.imprint","IMPRINT",FACE,{"disambiguationData":[TD([[makeQuery(id+"F9.imprint","IMPRINT",EDGE,{"derivedFrom":subQ2}),1.0]])]});}
            extrude(context, id + "F10", {"entities" : qUnion([Q0, Q1, Q2, Q3, Q4, Q5, Q6, Q7, Q8, Q9, Q10, Q11, Q12, Q13, Q14, Q15, Q16, Q17, Q18, Q19, Q20, Q21, Q22, Q23, Q24, Q25, Q26, Q27, Q28, Q29, Q30, Q31, Q32, Q33, Q34, Q35, Q36, Q37, Q38, Q39, Q40, Q41, Q42, Q43, Q44, Q45, Q46, Q47, Q48, Q49, Q50]), "oppositeDirection" : true, "depth" : 5 * mm});
        }
        {
            var Q0;
            Q0=qCreatedBy(makeId("Front.planeOp"),FACE);
            var sketch = newSketch(context, id + "F11", { "sketchPlane" : qUnion([Q0])});
            skLineSegment(sketch, "E19.0", {"start": v(0, -30.5) * mm, "end": v(0, 30.5) * mm});
            skLineSegment(sketch, "E19.1", {"start": v(0, -31.75) * mm, "end": v(0, 31.75) * mm});
            skLineSegment(sketch, "E19.2", {"start": v(0, -33) * mm, "end": v(0, 33) * mm});
            skLineSegment(sketch, "E20.bottom", {"start": v(0, 33) * mm, "end": v(5, 33) * mm});
            skLineSegment(sketch, "E20.top", {"start": v(0, 30.5) * mm, "end": v(5, 30.5) * mm});
            skLineSegment(sketch, "E20.left", {"start": v(0, 33) * mm, "end": v(0, 30.5) * mm});
            skLineSegment(sketch, "E20.right", {"start": v(5, 33) * mm, "end": v(5, 30.5) * mm});
            skLineSegment(sketch, "E21", {"start": v(2.5, 33) * mm, "end": v(2.5, 30.5) * mm, "construction": true});
            skLineSegment(sketch, "E22", {"start": v(0, 30.5) * mm, "end": v(10, 30.5) * mm, "construction": true});
            skArc(sketch, "E23", {"start": v(0.24, 33) * mm, "mid": v(0.1, 32.38) * mm, "end": v(0, 31.75) * mm});
            skArc(sketch, "E24.0.MirrorCS", {"start": v(4.76, 33) * mm, "mid": v(4.9, 32.38) * mm, "end": v(5, 31.75) * mm});
            skLineSegment(sketch, "E25", {"start": v(0, 0) * mm, "end": v(11.63, 0) * mm, "construction": true});
            skSolve(sketch);
        }
        {
            var Q0;
            {var subQ0=sQuery(id+"F11.wireOp",EDGE,"E23");Q0=makeQuery(id+"F11.imprint","IMPRINT",FACE,{"disambiguationData":[TD([[makeQuery(id+"F11.imprint","IMPRINT",EDGE,{"derivedFrom":subQ0}),-1.0]])]});}
            var Q1;
            {var subQ0=sQuery(id+"F11.wireOp",EDGE,"E24.0.MirrorCS");Q1=makeQuery(id+"F11.imprint","IMPRINT",FACE,{"disambiguationData":[TD([[makeQuery(id+"F11.imprint","IMPRINT",EDGE,{"derivedFrom":subQ0}),1.0]])]});}
            var Q2;
            Q2=sQuery(id+"F11.wireOp",EDGE,"E25");
            revolve(context, id + "F12", {"operationType" : NewBodyOperationType.REMOVE, "entities" : qUnion([Q0, Q1]), "axis" : qUnion([Q2]), "revolveType" : RevolveType.FULL, "oppositeDirection" : true});
        }
        {
            var Q0;
            Q0=makeQuery(id+"F10.opExtrude","CAP_FACE",FACE,{"disambiguationData":[OSD([sQuery(id+"F5.wireOp",EDGE,"E3"),sQuery(id+"F9.wireOp",EDGE,"E7"),sQuery(id+"F9.wireOp",EDGE,"E8"),sQuery(id+"F9.wireOp",EDGE,"E13"),sQuery(id+"F9.wireOp",EDGE,"E14.1.0"),sQuery(id+"F9.wireOp",EDGE,"E14.2.0"),sQuery(id+"F9.wireOp",EDGE,"E16"),sQuery(id+"F9.wireOp",EDGE,"E17.0.MirrorCS"),sQuery(id+"F9.wireOp",EDGE,"E18.1.0"),sQuery(id+"F9.wireOp",EDGE,"E18.1.1"),sQuery(id+"F9.wireOp",EDGE,"E18.2.0"),sQuery(id+"F9.wireOp",EDGE,"E18.2.1"),sQuery(id+"F9.wireOp",EDGE,"E18.3.0"),sQuery(id+"F9.wireOp",EDGE,"E18.3.1"),sQuery(id+"F9.wireOp",EDGE,"E18.4.0"),sQuery(id+"F9.wireOp",EDGE,"E18.4.1"),sQuery(id+"F9.wireOp",EDGE,"E18.5.0"),sQuery(id+"F9.wireOp",EDGE,"E18.5.1"),sQuery(id+"F9.wireOp",EDGE,"E18.6.0"),sQuery(id+"F9.wireOp",EDGE,"E18.6.1"),sQuery(id+"F9.wireOp",EDGE,"E18.7.0"),sQuery(id+"F9.wireOp",EDGE,"E18.7.1"),sQuery(id+"F9.wireOp",EDGE,"E18.8.0"),sQuery(id+"F9.wireOp",EDGE,"E18.8.1"),sQuery(id+"F9.wireOp",EDGE,"E18.9.0"),sQuery(id+"F9.wireOp",EDGE,"E18.9.1"),sQuery(id+"F9.wireOp",EDGE,"E18.10.0"),sQuery(id+"F9.wireOp",EDGE,"E18.10.1"),sQuery(id+"F9.wireOp",EDGE,"E18.11.0"),sQuery(id+"F9.wireOp",EDGE,"E18.11.1"),sQuery(id+"F9.wireOp",EDGE,"E18.12.0"),sQuery(id+"F9.wireOp",EDGE,"E18.12.1"),sQuery(id+"F9.wireOp",EDGE,"E18.13.0"),sQuery(id+"F9.wireOp",EDGE,"E18.13.1"),sQuery(id+"F9.wireOp",EDGE,"E18.14.0"),sQuery(id+"F9.wireOp",EDGE,"E18.14.1"),sQuery(id+"F9.wireOp",EDGE,"E18.15.0"),sQuery(id+"F9.wireOp",EDGE,"E18.15.1"),sQuery(id+"F9.wireOp",EDGE,"E18.16.0"),sQuery(id+"F9.wireOp",EDGE,"E18.16.1"),sQuery(id+"F9.wireOp",EDGE,"E18.17.0"),sQuery(id+"F9.wireOp",EDGE,"E18.17.1"),sQuery(id+"F9.wireOp",EDGE,"E18.18.0"),sQuery(id+"F9.wireOp",EDGE,"E18.18.1"),sQuery(id+"F9.wireOp",EDGE,"E18.19.0"),sQuery(id+"F9.wireOp",EDGE,"E18.19.1"),sQuery(id+"F9.wireOp",EDGE,"E18.20.0"),sQuery(id+"F9.wireOp",EDGE,"E18.20.1"),sQuery(id+"F9.wireOp",EDGE,"E18.21.0"),sQuery(id+"F9.wireOp",EDGE,"E18.21.1"),sQuery(id+"F9.wireOp",EDGE,"E18.22.0"),sQuery(id+"F9.wireOp",EDGE,"E18.22.1"),sQuery(id+"F9.wireOp",EDGE,"E18.23.0"),sQuery(id+"F9.wireOp",EDGE,"E18.23.1"),sQuery(id+"F9.wireOp",EDGE,"E18.24.0"),sQuery(id+"F9.wireOp",EDGE,"E18.24.1"),sQuery(id+"F9.wireOp",EDGE,"E18.25.0"),sQuery(id+"F9.wireOp",EDGE,"E18.25.1"),sQuery(id+"F9.wireOp",EDGE,"E18.26.0"),sQuery(id+"F9.wireOp",EDGE,"E18.26.1"),sQuery(id+"F9.wireOp",EDGE,"E18.27.0"),sQuery(id+"F9.wireOp",EDGE,"E18.27.1"),sQuery(id+"F9.wireOp",EDGE,"E18.28.0"),sQuery(id+"F9.wireOp",EDGE,"E18.28.1"),sQuery(id+"F9.wireOp",EDGE,"E18.29.0"),sQuery(id+"F9.wireOp",EDGE,"E18.29.1"),sQuery(id+"F9.wireOp",EDGE,"E18.30.0"),sQuery(id+"F9.wireOp",EDGE,"E18.30.1"),sQuery(id+"F9.wireOp",EDGE,"E18.31.0"),sQuery(id+"F9.wireOp",EDGE,"E18.31.1"),sQuery(id+"F9.wireOp",EDGE,"E18.32.0"),sQuery(id+"F9.wireOp",EDGE,"E18.32.1"),sQuery(id+"F9.wireOp",EDGE,"E18.33.0"),sQuery(id+"F9.wireOp",EDGE,"E18.33.1"),sQuery(id+"F9.wireOp",EDGE,"E18.34.0"),sQuery(id+"F9.wireOp",EDGE,"E18.34.1"),sQuery(id+"F9.wireOp",EDGE,"E18.35.0"),sQuery(id+"F9.wireOp",EDGE,"E18.35.1"),sQuery(id+"F9.wireOp",EDGE,"E18.36.0"),sQuery(id+"F9.wireOp",EDGE,"E18.36.1"),sQuery(id+"F9.wireOp",EDGE,"E18.37.0"),sQuery(id+"F9.wireOp",EDGE,"E18.37.1"),sQuery(id+"F9.wireOp",EDGE,"E18.38.0"),sQuery(id+"F9.wireOp",EDGE,"E18.38.1"),sQuery(id+"F9.wireOp",EDGE,"E18.39.0"),sQuery(id+"F9.wireOp",EDGE,"E18.39.1"),sQuery(id+"F9.wireOp",EDGE,"E18.40.0"),sQuery(id+"F9.wireOp",EDGE,"E18.40.1"),sQuery(id+"F9.wireOp",EDGE,"E18.41.0"),sQuery(id+"F9.wireOp",EDGE,"E18.41.1"),sQuery(id+"F9.wireOp",EDGE,"E18.42.0"),sQuery(id+"F9.wireOp",EDGE,"E18.42.1"),sQuery(id+"F9.wireOp",EDGE,"E18.43.0"),sQuery(id+"F9.wireOp",EDGE,"E18.43.1"),sQuery(id+"F9.wireOp",EDGE,"E18.44.0"),sQuery(id+"F9.wireOp",EDGE,"E18.44.1"),sQuery(id+"F9.wireOp",EDGE,"E18.45.0"),sQuery(id+"F9.wireOp",EDGE,"E18.45.1"),sQuery(id+"F9.wireOp",EDGE,"E18.46.0"),sQuery(id+"F9.wireOp",EDGE,"E18.46.1"),sQuery(id+"F9.wireOp",EDGE,"E18.47.0"),sQuery(id+"F9.wireOp",EDGE,"E18.47.1"),sQuery(id+"F9.wireOp",EDGE,"E18.48.0"),sQuery(id+"F9.wireOp",EDGE,"E18.48.1"),sQuery(id+"F9.wireOp",EDGE,"E18.49.0"),sQuery(id+"F9.wireOp",EDGE,"E18.49.1")])],"isStart":true});
            var sketch = newSketch(context, id + "F13", { "sketchPlane" : qUnion([Q0])});
            skCircle(sketch, "E26.0", {"center": v(0, 0) * mm, "radius": 4.5 * mm});
            skCircle(sketch, "E26.1", {"center": v(0, 0) * mm, "radius": 8 * mm});
            skCircle(sketch, "E26.2", {"center": v(-8.66, 5) * mm, "radius": 1.25 * mm});
            skCircle(sketch, "E26.3", {"center": v(8.66, 5) * mm, "radius": 1.25 * mm});
            skCircle(sketch, "E26.4", {"center": v(0, -10) * mm, "radius": 1.25 * mm});
            skCircle(sketch, "E27", {"center": v(0, 0) * mm, "radius": 6.5 * mm});
            skCircle(sketch, "E28", {"center": v(0, 0) * mm, "radius": 12.5 * mm});
            skSolve(sketch);
        }
        {
            var Q0;
            Q0=makeQuery(id+"F13.imprint","IMPRINT",FACE,{"disambiguationData":[TD([[makeQuery(id+"F13.imprint","IMPRINT",EDGE,{"derivedFrom":sQuery(id+"F13.wireOp",EDGE,"E26.0")}),-1.0]])]});
            extrude(context, id + "F14", {"entities" : qUnion([Q0]), "oppositeDirection" : true, "depth" : 6.5 * mm});
        }
        {
            var Q0;
            Q0=makeQuery(id+"F13.imprint","IMPRINT",FACE,{"disambiguationData":[TD([[makeQuery(id+"F13.imprint","IMPRINT",EDGE,{"derivedFrom":sQuery(id+"F13.wireOp",EDGE,"E26.1")}),1.0]])]});
            extrude(context, id + "F15", {"entities" : qUnion([Q0]), "operationType" : NewBodyOperationType.ADD, "oppositeDirection" : true, "depth" : 5 * mm});
        }
        {
            var Q0;
            Q0=makeQuery(id+"F13.imprint","IMPRINT",FACE,{"disambiguationData":[TD([[makeQuery(id+"F13.imprint","IMPRINT",EDGE,{"derivedFrom":sQuery(id+"F13.wireOp",EDGE,"E26.0")}),-1.0]])]});
            extrude(context, id + "F16", {"entities" : qUnion([Q0]), "operationType" : NewBodyOperationType.ADD, "depth" : 6.5 * mm});
        }
        {
            var Q0;
            Q0=makeQuery(id+"F13.imprint","IMPRINT",FACE,{"disambiguationData":[TD([[makeQuery(id+"F13.imprint","IMPRINT",EDGE,{"derivedFrom":sQuery(id+"F13.wireOp",EDGE,"E26.1")}),-1.0]])]});
            var Q1;
            Q1=makeQuery(id+"F13.imprint","IMPRINT",FACE,{"disambiguationData":[TD([[makeQuery(id+"F13.imprint","IMPRINT",EDGE,{"derivedFrom":sQuery(id+"F13.wireOp",EDGE,"E26.1")}),1.0]])]});
            extrude(context, id + "F17", {"entities" : qUnion([Q0, Q1]), "operationType" : NewBodyOperationType.ADD, "depth" : 1.5 * mm});
        }
        {
            var Q0;
            Q0=makeQuery(id+"F17.opExtrude","CAP_FACE",FACE,{"disambiguationData":[OSD([sQuery(id+"F13.wireOp",EDGE,"E26.2"),sQuery(id+"F13.wireOp",EDGE,"E26.3"),sQuery(id+"F13.wireOp",EDGE,"E26.4"),sQuery(id+"F13.wireOp",EDGE,"E27"),sQuery(id+"F13.wireOp",EDGE,"E28")])],"isStart":false});
            var sketch = newSketch(context, id + "F18", { "sketchPlane" : qUnion([Q0])});
            skCircle(sketch, "E29", {"center": v(0, 0) * mm, "radius": 14.5 * mm});
            skCircle(sketch, "E30", {"center": v(0, 0) * mm, "radius": 17 * mm});
            skCircle(sketch, "E31", {"center": v(0, 0) * mm, "radius": 15.75 * mm, "construction": true});
            skLineSegment(sketch, "E32", {"start": v(0, 0) * mm, "end": v(0, 17) * mm, "construction": true});
            skLineSegment(sketch, "E33", {"start": v(0, 0) * mm, "end": v(-0.99, 15.72) * mm, "construction": true});
            skLineSegment(sketch, "E34", {"start": v(0, 14.5) * mm, "end": v(15, 14.5) * mm, "construction": true});
            skArc(sketch, "E35", {"start": v(-0.84, 16.98) * mm, "mid": v(-0.99, 15.72) * mm, "end": v(-1.04, 14.46) * mm});
            skArc(sketch, "E36.0.MirrorCS", {"start": v(0.84, 16.98) * mm, "mid": v(0.99, 15.72) * mm, "end": v(1.04, 14.46) * mm});
            skArc(sketch, "E37.1.0", {"start": v(-5.04, 16.24) * mm, "mid": v(-4.87, 14.98) * mm, "end": v(-4.6, 13.75) * mm});
            skArc(sketch, "E37.1.1", {"start": v(-3.4, 16.66) * mm, "mid": v(-2.95, 15.48) * mm, "end": v(-2.6, 14.27) * mm});
            skArc(sketch, "E37.2.0", {"start": v(-8.92, 14.47) * mm, "mid": v(-8.44, 13.3) * mm, "end": v(-7.87, 12.18) * mm});
            skArc(sketch, "E37.2.1", {"start": v(-7.44, 15.28) * mm, "mid": v(-6.7, 14.26) * mm, "end": v(-6.06, 13.17) * mm});
            skArc(sketch, "E37.3.0", {"start": v(-12.24, 11.8) * mm, "mid": v(-11.48, 10.79) * mm, "end": v(-10.66, 9.83) * mm});
            skArc(sketch, "E37.3.1", {"start": v(-11, 12.95) * mm, "mid": v(-10.04, 12.14) * mm, "end": v(-9.15, 11.25) * mm});
            skArc(sketch, "E37.4.0", {"start": v(-14.79, 8.39) * mm, "mid": v(-13.8, 7.6) * mm, "end": v(-12.77, 6.88) * mm});
            skArc(sketch, "E37.4.1", {"start": v(-13.88, 9.8) * mm, "mid": v(-12.75, 9.26) * mm, "end": v(-11.66, 8.62) * mm});
            skArc(sketch, "E37.5.0", {"start": v(-16.4, 4.45) * mm, "mid": v(-15.26, 3.92) * mm, "end": v(-14.08, 3.48) * mm});
            skArc(sketch, "E37.5.1", {"start": v(-15.89, 6.05) * mm, "mid": v(-14.65, 5.8) * mm, "end": v(-13.44, 5.45) * mm});
            skArc(sketch, "E37.6.0", {"start": v(-17, 0.23) * mm, "mid": v(-15.76, 0) * mm, "end": v(-14.5, -0.13) * mm});
            skArc(sketch, "E37.6.1", {"start": v(-16.9, 1.9) * mm, "mid": v(-15.63, 1.97) * mm, "end": v(-14.37, 1.94) * mm});
            skArc(sketch, "E37.7.0", {"start": v(-16.52, -4) * mm, "mid": v(-15.26, -3.92) * mm, "end": v(-14.01, -3.73) * mm});
            skArc(sketch, "E37.7.1", {"start": v(-16.84, -2.35) * mm, "mid": v(-15.63, -1.98) * mm, "end": v(-14.4, -1.7) * mm});
            skArc(sketch, "E37.8.0", {"start": v(-15, -8) * mm, "mid": v(-13.8, -7.59) * mm, "end": v(-12.65, -7.1) * mm});
            skArc(sketch, "E37.8.1", {"start": v(-15.72, -6.47) * mm, "mid": v(-14.65, -5.8) * mm, "end": v(-13.53, -5.22) * mm});
            skArc(sketch, "E37.9.0", {"start": v(-12.55, -11.47) * mm, "mid": v(-11.49, -10.79) * mm, "end": v(-10.48, -10.02) * mm});
            skArc(sketch, "E37.9.1", {"start": v(-13.62, -10.17) * mm, "mid": v(-12.75, -9.26) * mm, "end": v(-11.8, -8.42) * mm});
            skArc(sketch, "E37.10.0", {"start": v(-9.3, -14.23) * mm, "mid": v(-8.44, -13.3) * mm, "end": v(-7.66, -12.3) * mm});
            skArc(sketch, "E37.10.1", {"start": v(-10.66, -13.24) * mm, "mid": v(-10.04, -12.14) * mm, "end": v(-9.34, -11.1) * mm});
            skArc(sketch, "E37.11.0", {"start": v(-5.47, -16.1) * mm, "mid": v(-4.87, -14.98) * mm, "end": v(-4.36, -13.83) * mm});
            skArc(sketch, "E37.11.1", {"start": v(-7.03, -15.48) * mm, "mid": v(-6.7, -14.26) * mm, "end": v(-6.29, -13.07) * mm});
            skArc(sketch, "E37.12.0", {"start": v(-1.3, -16.95) * mm, "mid": v(-1, -15.72) * mm, "end": v(-0.79, -14.48) * mm});
            skArc(sketch, "E37.12.1", {"start": v(-2.96, -16.74) * mm, "mid": v(-2.95, -15.48) * mm, "end": v(-2.84, -14.22) * mm});
            skArc(sketch, "E37.13.0", {"start": v(2.96, -16.74) * mm, "mid": v(2.95, -15.48) * mm, "end": v(2.84, -14.22) * mm});
            skArc(sketch, "E37.13.1", {"start": v(1.3, -16.95) * mm, "mid": v(1, -15.72) * mm, "end": v(0.79, -14.48) * mm});
            skArc(sketch, "E37.14.0", {"start": v(7.03, -15.48) * mm, "mid": v(6.7, -14.26) * mm, "end": v(6.29, -13.07) * mm});
            skArc(sketch, "E37.14.1", {"start": v(5.47, -16.1) * mm, "mid": v(4.87, -14.98) * mm, "end": v(4.36, -13.83) * mm});
            skArc(sketch, "E37.15.0", {"start": v(10.66, -13.24) * mm, "mid": v(10.04, -12.14) * mm, "end": v(9.34, -11.1) * mm});
            skArc(sketch, "E37.15.1", {"start": v(9.3, -14.23) * mm, "mid": v(8.44, -13.3) * mm, "end": v(7.66, -12.3) * mm});
            skArc(sketch, "E37.16.0", {"start": v(13.62, -10.17) * mm, "mid": v(12.75, -9.26) * mm, "end": v(11.8, -8.42) * mm});
            skArc(sketch, "E37.16.1", {"start": v(12.55, -11.47) * mm, "mid": v(11.49, -10.79) * mm, "end": v(10.48, -10.02) * mm});
            skArc(sketch, "E37.17.0", {"start": v(15.72, -6.47) * mm, "mid": v(14.65, -5.8) * mm, "end": v(13.53, -5.22) * mm});
            skArc(sketch, "E37.17.1", {"start": v(15, -8) * mm, "mid": v(13.8, -7.59) * mm, "end": v(12.65, -7.1) * mm});
            skArc(sketch, "E37.18.0", {"start": v(16.84, -2.35) * mm, "mid": v(15.63, -1.98) * mm, "end": v(14.4, -1.7) * mm});
            skArc(sketch, "E37.18.1", {"start": v(16.52, -4) * mm, "mid": v(15.26, -3.92) * mm, "end": v(14.01, -3.73) * mm});
            skArc(sketch, "E37.19.0", {"start": v(16.9, 1.9) * mm, "mid": v(15.63, 1.97) * mm, "end": v(14.37, 1.94) * mm});
            skArc(sketch, "E37.19.1", {"start": v(17, 0.23) * mm, "mid": v(15.76, 0) * mm, "end": v(14.5, -0.13) * mm});
            skArc(sketch, "E37.20.0", {"start": v(15.89, 6.05) * mm, "mid": v(14.65, 5.8) * mm, "end": v(13.44, 5.45) * mm});
            skArc(sketch, "E37.20.1", {"start": v(16.4, 4.45) * mm, "mid": v(15.26, 3.92) * mm, "end": v(14.08, 3.48) * mm});
            skArc(sketch, "E37.21.0", {"start": v(13.88, 9.8) * mm, "mid": v(12.75, 9.26) * mm, "end": v(11.66, 8.62) * mm});
            skArc(sketch, "E37.21.1", {"start": v(14.79, 8.39) * mm, "mid": v(13.8, 7.6) * mm, "end": v(12.77, 6.88) * mm});
            skArc(sketch, "E37.22.0", {"start": v(11, 12.95) * mm, "mid": v(10.04, 12.14) * mm, "end": v(9.15, 11.25) * mm});
            skArc(sketch, "E37.22.1", {"start": v(12.24, 11.8) * mm, "mid": v(11.48, 10.79) * mm, "end": v(10.66, 9.83) * mm});
            skArc(sketch, "E37.23.0", {"start": v(7.44, 15.28) * mm, "mid": v(6.7, 14.26) * mm, "end": v(6.06, 13.17) * mm});
            skArc(sketch, "E37.23.1", {"start": v(8.92, 14.47) * mm, "mid": v(8.44, 13.3) * mm, "end": v(7.87, 12.18) * mm});
            skArc(sketch, "E37.24.0", {"start": v(3.4, 16.66) * mm, "mid": v(2.95, 15.48) * mm, "end": v(2.6, 14.27) * mm});
            skArc(sketch, "E37.24.1", {"start": v(5.04, 16.24) * mm, "mid": v(4.87, 14.98) * mm, "end": v(4.6, 13.75) * mm});
            skSolve(sketch);
        }
        {
            var Q0;
            Q0=makeQuery(id+"F18.imprint","IMPRINT",FACE,{"disambiguationData":[TD([[makeQuery(id+"F18.imprint","IMPRINT",EDGE,{"derivedFrom":makeQuery(id+"F17.opExtrude","CAP_EDGE",EDGE,{"disambiguationData":[OSD([sQuery(id+"F13.wireOp",EDGE,"E26.2")])],"isStart":false})}),-1.0]])]});
            var Q1;
            Q1=makeQuery(id+"F18.imprint","IMPRINT",FACE,{"disambiguationData":[TD([[makeQuery(id+"F18.imprint","IMPRINT",EDGE,{"derivedFrom":makeQuery(id+"F17.opExtrude","CAP_EDGE",EDGE,{"disambiguationData":[OSD([sQuery(id+"F13.wireOp",EDGE,"E28")])],"isStart":false})}),-1.0]])]});
            var Q2;
            {var subQ1=sQuery(id+"F18.wireOp",EDGE,"E35");Q2=makeQuery(id+"F18.imprint","IMPRINT",FACE,{"disambiguationData":[TD([[makeQuery(id+"F18.imprint","IMPRINT",EDGE,{"derivedFrom":subQ1}),1.0]])]});}
            var Q3;
            {var subQ1=sQuery(id+"F18.wireOp",EDGE,"E37.1.0");Q3=makeQuery(id+"F18.imprint","IMPRINT",FACE,{"disambiguationData":[TD([[makeQuery(id+"F18.imprint","IMPRINT",EDGE,{"derivedFrom":subQ1}),1.0]])]});}
            var Q4;
            {var subQ1=sQuery(id+"F18.wireOp",EDGE,"E37.2.0");Q4=makeQuery(id+"F18.imprint","IMPRINT",FACE,{"disambiguationData":[TD([[makeQuery(id+"F18.imprint","IMPRINT",EDGE,{"derivedFrom":subQ1}),1.0]])]});}
            var Q5;
            {var subQ1=sQuery(id+"F18.wireOp",EDGE,"E37.3.0");Q5=makeQuery(id+"F18.imprint","IMPRINT",FACE,{"disambiguationData":[TD([[makeQuery(id+"F18.imprint","IMPRINT",EDGE,{"derivedFrom":subQ1}),1.0]])]});}
            var Q6;
            {var subQ1=sQuery(id+"F18.wireOp",EDGE,"E37.4.0");Q6=makeQuery(id+"F18.imprint","IMPRINT",FACE,{"disambiguationData":[TD([[makeQuery(id+"F18.imprint","IMPRINT",EDGE,{"derivedFrom":subQ1}),1.0]])]});}
            var Q7;
            {var subQ1=sQuery(id+"F18.wireOp",EDGE,"E37.5.0");Q7=makeQuery(id+"F18.imprint","IMPRINT",FACE,{"disambiguationData":[TD([[makeQuery(id+"F18.imprint","IMPRINT",EDGE,{"derivedFrom":subQ1}),1.0]])]});}
            var Q8;
            {var subQ1=sQuery(id+"F18.wireOp",EDGE,"E37.6.0");Q8=makeQuery(id+"F18.imprint","IMPRINT",FACE,{"disambiguationData":[TD([[makeQuery(id+"F18.imprint","IMPRINT",EDGE,{"derivedFrom":subQ1}),1.0]])]});}
            var Q9;
            {var subQ1=sQuery(id+"F18.wireOp",EDGE,"E37.7.0");Q9=makeQuery(id+"F18.imprint","IMPRINT",FACE,{"disambiguationData":[TD([[makeQuery(id+"F18.imprint","IMPRINT",EDGE,{"derivedFrom":subQ1}),1.0]])]});}
            var Q10;
            {var subQ1=sQuery(id+"F18.wireOp",EDGE,"E37.8.0");Q10=makeQuery(id+"F18.imprint","IMPRINT",FACE,{"disambiguationData":[TD([[makeQuery(id+"F18.imprint","IMPRINT",EDGE,{"derivedFrom":subQ1}),1.0]])]});}
            var Q11;
            {var subQ1=sQuery(id+"F18.wireOp",EDGE,"E37.9.0");Q11=makeQuery(id+"F18.imprint","IMPRINT",FACE,{"disambiguationData":[TD([[makeQuery(id+"F18.imprint","IMPRINT",EDGE,{"derivedFrom":subQ1}),1.0]])]});}
            var Q12;
            {var subQ1=sQuery(id+"F18.wireOp",EDGE,"E37.10.0");Q12=makeQuery(id+"F18.imprint","IMPRINT",FACE,{"disambiguationData":[TD([[makeQuery(id+"F18.imprint","IMPRINT",EDGE,{"derivedFrom":subQ1}),1.0]])]});}
            var Q13;
            {var subQ1=sQuery(id+"F18.wireOp",EDGE,"E37.11.0");Q13=makeQuery(id+"F18.imprint","IMPRINT",FACE,{"disambiguationData":[TD([[makeQuery(id+"F18.imprint","IMPRINT",EDGE,{"derivedFrom":subQ1}),1.0]])]});}
            var Q14;
            {var subQ1=sQuery(id+"F18.wireOp",EDGE,"E37.12.0");Q14=makeQuery(id+"F18.imprint","IMPRINT",FACE,{"disambiguationData":[TD([[makeQuery(id+"F18.imprint","IMPRINT",EDGE,{"derivedFrom":subQ1}),1.0]])]});}
            var Q15;
            {var subQ1=sQuery(id+"F18.wireOp",EDGE,"E37.13.0");Q15=makeQuery(id+"F18.imprint","IMPRINT",FACE,{"disambiguationData":[TD([[makeQuery(id+"F18.imprint","IMPRINT",EDGE,{"derivedFrom":subQ1}),1.0]])]});}
            var Q16;
            {var subQ1=sQuery(id+"F18.wireOp",EDGE,"E37.14.0");Q16=makeQuery(id+"F18.imprint","IMPRINT",FACE,{"disambiguationData":[TD([[makeQuery(id+"F18.imprint","IMPRINT",EDGE,{"derivedFrom":subQ1}),1.0]])]});}
            var Q17;
            {var subQ1=sQuery(id+"F18.wireOp",EDGE,"E37.15.0");Q17=makeQuery(id+"F18.imprint","IMPRINT",FACE,{"disambiguationData":[TD([[makeQuery(id+"F18.imprint","IMPRINT",EDGE,{"derivedFrom":subQ1}),1.0]])]});}
            var Q18;
            {var subQ0=sQuery(id+"F18.wireOp",EDGE,"E37.16.0");Q18=makeQuery(id+"F18.imprint","IMPRINT",FACE,{"disambiguationData":[TD([[makeQuery(id+"F18.imprint","IMPRINT",EDGE,{"derivedFrom":subQ0}),1.0]])]});}
            var Q19;
            {var subQ1=sQuery(id+"F18.wireOp",EDGE,"E37.17.0");Q19=makeQuery(id+"F18.imprint","IMPRINT",FACE,{"disambiguationData":[TD([[makeQuery(id+"F18.imprint","IMPRINT",EDGE,{"derivedFrom":subQ1}),1.0]])]});}
            var Q20;
            {var subQ1=sQuery(id+"F18.wireOp",EDGE,"E37.18.0");Q20=makeQuery(id+"F18.imprint","IMPRINT",FACE,{"disambiguationData":[TD([[makeQuery(id+"F18.imprint","IMPRINT",EDGE,{"derivedFrom":subQ1}),1.0]])]});}
            var Q21;
            {var subQ0=sQuery(id+"F18.wireOp",EDGE,"E37.19.0");Q21=makeQuery(id+"F18.imprint","IMPRINT",FACE,{"disambiguationData":[TD([[makeQuery(id+"F18.imprint","IMPRINT",EDGE,{"derivedFrom":subQ0}),1.0]])]});}
            var Q22;
            {var subQ1=sQuery(id+"F18.wireOp",EDGE,"E37.20.0");Q22=makeQuery(id+"F18.imprint","IMPRINT",FACE,{"disambiguationData":[TD([[makeQuery(id+"F18.imprint","IMPRINT",EDGE,{"derivedFrom":subQ1}),1.0]])]});}
            var Q23;
            {var subQ1=sQuery(id+"F18.wireOp",EDGE,"E37.21.0");Q23=makeQuery(id+"F18.imprint","IMPRINT",FACE,{"disambiguationData":[TD([[makeQuery(id+"F18.imprint","IMPRINT",EDGE,{"derivedFrom":subQ1}),1.0]])]});}
            var Q24;
            {var subQ1=sQuery(id+"F18.wireOp",EDGE,"E37.22.0");Q24=makeQuery(id+"F18.imprint","IMPRINT",FACE,{"disambiguationData":[TD([[makeQuery(id+"F18.imprint","IMPRINT",EDGE,{"derivedFrom":subQ1}),1.0]])]});}
            var Q25;
            {var subQ1=sQuery(id+"F18.wireOp",EDGE,"E37.23.0");Q25=makeQuery(id+"F18.imprint","IMPRINT",FACE,{"disambiguationData":[TD([[makeQuery(id+"F18.imprint","IMPRINT",EDGE,{"derivedFrom":subQ1}),1.0]])]});}
            var Q26;
            {var subQ1=sQuery(id+"F18.wireOp",EDGE,"E37.24.0");Q26=makeQuery(id+"F18.imprint","IMPRINT",FACE,{"disambiguationData":[TD([[makeQuery(id+"F18.imprint","IMPRINT",EDGE,{"derivedFrom":subQ1}),1.0]])]});}
            extrude(context, id + "F19", {"entities" : qUnion([Q0, Q1, Q2, Q3, Q4, Q5, Q6, Q7, Q8, Q9, Q10, Q11, Q12, Q13, Q14, Q15, Q16, Q17, Q18, Q19, Q20, Q21, Q22, Q23, Q24, Q25, Q26]), "depth" : 5 * mm});
        }
        {
            var Q0;
            Q0=makeQuery(id+"F19.opExtrude","CAP_EDGE",EDGE,{"disambiguationData":[OSD([sQuery(id+"F13.wireOp",EDGE,"E26.2")])],"isStart":false});
            var Q1;
            Q1=makeQuery(id+"F19.opExtrude","CAP_EDGE",EDGE,{"disambiguationData":[OSD([sQuery(id+"F13.wireOp",EDGE,"E26.3")])],"isStart":false});
            var Q2;
            Q2=makeQuery(id+"F19.opExtrude","CAP_EDGE",EDGE,{"disambiguationData":[OSD([sQuery(id+"F13.wireOp",EDGE,"E26.4")])],"isStart":false});
            chamfer(context, id + "F20", {"entities" : qUnion([Q0, Q1, Q2]), "width" : 1.25 * mm, "tangentPropagation" : true});
        }
        {
            var Q0;
            Q0=qCreatedBy(makeId("Front.planeOp"),FACE);
            var sketch = newSketch(context, id + "F21", { "sketchPlane" : qUnion([Q0])});
            skLineSegment(sketch, "E38.0", {"start": v(-1.5, -14.5) * mm, "end": v(-1.5, 14.5) * mm});
            skLineSegment(sketch, "E38.1", {"start": v(-1.5, -15.75) * mm, "end": v(-1.5, 15.75) * mm});
            skLineSegment(sketch, "E38.2", {"start": v(-1.5, -17) * mm, "end": v(-1.5, 17) * mm});
            skLineSegment(sketch, "E39.bottom", {"start": v(-1.5, 17) * mm, "end": v(-6.5, 17) * mm});
            skLineSegment(sketch, "E39.top", {"start": v(-1.5, 14.5) * mm, "end": v(-6.5, 14.5) * mm});
            skLineSegment(sketch, "E39.left", {"start": v(-1.5, 17) * mm, "end": v(-1.5, 14.5) * mm});
            skLineSegment(sketch, "E39.right", {"start": v(-6.5, 17) * mm, "end": v(-6.5, 14.5) * mm});
            skLineSegment(sketch, "E40", {"start": v(-4, 17) * mm, "end": v(-4, 14.5) * mm, "construction": true});
            skLineSegment(sketch, "E41", {"start": v(-1.5, 14.5) * mm, "end": v(-11.5, 14.5) * mm, "construction": true});
            skArc(sketch, "E42", {"start": v(-1.5, 15.75) * mm, "mid": v(-1.6, 16.38) * mm, "end": v(-1.74, 17) * mm});
            skLineSegment(sketch, "E43", {"start": v(-1.5, 0) * mm, "end": v(-8.45, 0) * mm, "construction": true});
            skArc(sketch, "E44.0.MirrorCS", {"start": v(-6.5, 15.75) * mm, "mid": v(-6.4, 16.38) * mm, "end": v(-6.26, 17) * mm});
            skSolve(sketch);
        }
        {
            var Q0;
            {var subQ0=sQuery(id+"F21.wireOp",EDGE,"E42");Q0=makeQuery(id+"F21.imprint","IMPRINT",FACE,{"disambiguationData":[TD([[makeQuery(id+"F21.imprint","IMPRINT",EDGE,{"derivedFrom":subQ0}),-1.0]])]});}
            var Q1;
            {var subQ0=sQuery(id+"F21.wireOp",EDGE,"E44.0.MirrorCS");Q1=makeQuery(id+"F21.imprint","IMPRINT",FACE,{"disambiguationData":[TD([[makeQuery(id+"F21.imprint","IMPRINT",EDGE,{"derivedFrom":subQ0}),1.0]])]});}
            var Q2;
            Q2=sQuery(id+"F21.wireOp",EDGE,"E43");
            revolve(context, id + "F22", {"operationType" : NewBodyOperationType.REMOVE, "entities" : qUnion([Q0, Q1]), "axis" : qUnion([Q2]), "revolveType" : RevolveType.FULL, "oppositeDirection" : true});
        }
        {
            var Q0;
            Q0=makeQuery(id+"F2.opExtrude","CAP_EDGE",EDGE,{"disambiguationData":[OSD([sQuery(id+"F0.wireOp",EDGE,"E1")])],"isStart":false});
            var Q1;
            Q1=makeQuery(id+"F1.opExtrude","CAP_EDGE",EDGE,{"disambiguationData":[OSD([sQuery(id+"F0.wireOp",EDGE,"E0")])],"isStart":false});
            var Q2;
            Q2=makeQuery(id+"F17.opExtrude","CAP_EDGE",EDGE,{"disambiguationData":[OSD([sQuery(id+"F13.wireOp",EDGE,"E28")])],"isStart":true});
            var Q3;
            Q3=makeQuery(id+"F14.opExtrude","CAP_EDGE",EDGE,{"disambiguationData":[OSD([sQuery(id+"F13.wireOp",EDGE,"E27")])],"isStart":false});
            var Q4;
            Q4=makeQuery(id+"F17.opExtrude","CAP_EDGE",EDGE,{"disambiguationData":[OSD([sQuery(id+"F13.wireOp",EDGE,"E28")])],"isStart":false});
            chamfer(context, id + "F23", {"entities" : qUnion([Q0, Q1, Q2, Q3, Q4]), "width" : 0.2 * mm, "tangentPropagation" : true});
        }
    });
